annotation { "Feature Type Name" : "Feature", "Feature Type Description" : "" }
export const myFeature = defineFeature(function(context is Context, id is Id, definition is map)
    precondition{}
    {
        {
            var Q0;
            Q0=qCreatedBy(makeId("Top.planeOp"),FACE);
            var sketch = newSketch(context, id + "F0", { "sketchPlane" : qUnion([Q0])});
            skLineSegment(sketch, "E0.bottom", {"start": v(-906.5, 179.8) * mm, "end": v(731.8, 179.8) * mm});
            skLineSegment(sketch, "E0.top", {"start": v(-906.5, -706.02) * mm, "end": v(731.8, -706.02) * mm});
            skLineSegment(sketch, "E0.left", {"start": v(-906.5, 179.8) * mm, "end": v(-906.5, -706.02) * mm});
            skLineSegment(sketch, "E0.right", {"start": v(731.8, 179.8) * mm, "end": v(731.8, -706.02) * mm});
            skLineSegment(sketch, "E1.bottom", {"start": v(-379.45, 179.8) * mm, "end": v(-290.55, 179.8) * mm});
            skLineSegment(sketch, "E1.top", {"start": v(-379.45, -706.02) * mm, "end": v(-290.55, -706.02) * mm});
            skLineSegment(sketch, "E1.left", {"start": v(-379.45, 179.8) * mm, "end": v(-379.45, -706.02) * mm});
            skLineSegment(sketch, "E1.right", {"start": v(-290.55, 179.8) * mm, "end": v(-290.55, -706.02) * mm});
            skLineSegment(sketch, "E2.bottom", {"start": v(230.15, 179.8) * mm, "end": v(319.05, 179.8) * mm});
            skLineSegment(sketch, "E2.top", {"start": v(230.15, -706.02) * mm, "end": v(319.05, -706.02) * mm});
            skLineSegment(sketch, "E2.left", {"start": v(230.15, 179.8) * mm, "end": v(230.15, -706.02) * mm});
            skLineSegment(sketch, "E2.right", {"start": v(319.05, 179.8) * mm, "end": v(319.05, -706.02) * mm});
            skLineSegment(sketch, "E3.0", {"start": v(-919.2, 192.5) * mm, "end": v(744.5, 192.5) * mm});
            skLineSegment(sketch, "E3.1", {"start": v(-919.2, 192.5) * mm, "end": v(-919.2, -718.72) * mm});
            skLineSegment(sketch, "E3.2", {"start": v(-919.2, -718.72) * mm, "end": v(744.5, -718.72) * mm});
            skLineSegment(sketch, "E3.3", {"start": v(744.5, 192.5) * mm, "end": v(744.5, -718.72) * mm});
            skLineSegment(sketch, "E4", {"start": v(-906.5, -263.1) * mm, "end": v(731.8, -263.1) * mm, "construction": true});
            skLineSegment(sketch, "E5", {"start": v(-87.35, 192.5) * mm, "end": v(-87.35, -718.72) * mm, "construction": true});
            skLineSegment(sketch, "E6", {"start": v(-360.4, 192.5) * mm, "end": v(-360.4, -718.72) * mm, "construction": true});
            skLineSegment(sketch, "E7", {"start": v(185.7, 192.5) * mm, "end": v(185.7, -718.72) * mm, "construction": true});
            skSolve(sketch);
        }
        {
            var Q0;
            Q0=makeQuery(id+"F0.imprint","IMPRINT",FACE,{"disambiguationData":[TD([[makeQuery(id+"F0.imprint","IMPRINT",EDGE,{"derivedFrom":sQuery(id+"F0.wireOp",EDGE,"E1.bottom")}),-1.0]])]});
            var Q1;
            Q1=makeQuery(id+"F0.imprint","IMPRINT",FACE,{"disambiguationData":[TD([[makeQuery(id+"F0.imprint","IMPRINT",EDGE,{"derivedFrom":sQuery(id+"F0.wireOp",EDGE,"E2.bottom")}),-1.0]])]});
            var Q2;
            {var subQ1=sQuery(id+"F0.wireOp",EDGE,"E0.left");Q2=makeQuery(id+"F0.imprint","IMPRINT",FACE,{"disambiguationData":[TD([[makeQuery(id+"F0.imprint","IMPRINT",EDGE,{"derivedFrom":subQ1}),-1.0]])]});}
            extrude(context, id + "F1", {"entities" : qUnion([Q0, Q1, Q2]), "depth" : 88.9 * mm});
        }
        {
            var Q0;
            Q0=qCreatedBy(makeId("Top.planeOp"),FACE);
            var sketch = newSketch(context, id + "F2", { "sketchPlane" : qUnion([Q0])});
            skLineSegment(sketch, "E8.bottom", {"start": v(-914.83, 184.33) * mm, "end": v(738.67, 184.33) * mm});
            skLineSegment(sketch, "E8.top", {"start": v(-914.83, -709.72) * mm, "end": v(738.67, -709.72) * mm});
            skLineSegment(sketch, "E8.left", {"start": v(-914.83, 184.33) * mm, "end": v(-914.83, -709.72) * mm});
            skLineSegment(sketch, "E8.right", {"start": v(738.67, 184.33) * mm, "end": v(738.67, -709.72) * mm});
            skSolve(sketch);
        }
        {
            var Q0;
            Q0 = qSketchRegion(id + "F2", true);
            extrude(context, id + "F3", {"entities" : qUnion([Q0]), "oppositeDirection" : true, "depth" : 1.63 * mm});
        }
        {
            var Q0;
            Q0=qCreatedBy(makeId("Top.planeOp"),FACE);
            var sketch = newSketch(context, id + "F4", { "sketchPlane" : qUnion([Q0])});
            skLineSegment(sketch, "E9.bottom", {"start": v(-389.54, -366.33) * mm, "end": v(-713.39, -366.33) * mm});
            skLineSegment(sketch, "E9.top", {"start": v(-389.54, -156.78) * mm, "end": v(-624.62, -156.78) * mm});
            skLineSegment(sketch, "E9.left", {"start": v(-389.54, -366.33) * mm, "end": v(-389.54, -156.78) * mm});
            skLineSegment(sketch, "E9.right", {"start": v(-713.39, -366.33) * mm, "end": v(-713.39, -156.78) * mm});
            skCircle(sketch, "E10", {"center": v(-481.61, -261.55) * mm, "radius": 79.38 * mm});
            skLineSegment(sketch, "E11.top", {"start": v(-624.62, -193.13) * mm, "end": v(-687, -193.13) * mm});
            skLineSegment(sketch, "E11.left", {"start": v(-624.62, -156.78) * mm, "end": v(-624.62, -193.13) * mm});
            skLineSegment(sketch, "E11.right", {"start": v(-687, -156.78) * mm, "end": v(-687, -193.13) * mm});
            skLineSegment(sketch, "E12.trimOffspring", {"start": v(-687, -156.78) * mm, "end": v(-713.39, -156.78) * mm});
            skLineSegment(sketch, "E13.bottom", {"start": v(20.9, -171.42) * mm, "end": v(20.9, -495.27) * mm});
            skLineSegment(sketch, "E13.top", {"start": v(-188.66, -171.42) * mm, "end": v(-188.66, -406.5) * mm});
            skLineSegment(sketch, "E13.left", {"start": v(20.9, -171.42) * mm, "end": v(-188.66, -171.42) * mm});
            skLineSegment(sketch, "E13.right", {"start": v(20.9, -495.27) * mm, "end": v(-188.66, -495.27) * mm});
            skCircle(sketch, "E14", {"center": v(-83.88, -263.5) * mm, "radius": 79.38 * mm});
            skLineSegment(sketch, "E15.top", {"start": v(-152.3, -406.5) * mm, "end": v(-152.3, -468.9) * mm});
            skLineSegment(sketch, "E15.left", {"start": v(-188.66, -406.5) * mm, "end": v(-152.3, -406.5) * mm});
            skLineSegment(sketch, "E15.right", {"start": v(-188.66, -468.9) * mm, "end": v(-152.3, -468.9) * mm});
            skLineSegment(sketch, "E16.trimOffspring", {"start": v(-188.66, -468.9) * mm, "end": v(-188.66, -495.27) * mm});
            skSolve(sketch);
        }
        {
            var Q0;
            Q0=makeQuery(id+"F4.imprint","IMPRINT",FACE,{"disambiguationData":[TD([[makeQuery(id+"F4.imprint","IMPRINT",EDGE,{"derivedFrom":sQuery(id+"F4.wireOp",EDGE,"E9.bottom")}),-1.0]])]});
            var Q1;
            Q1=makeQuery(id+"F4.imprint","IMPRINT",FACE,{"disambiguationData":[TD([[makeQuery(id+"F4.imprint","IMPRINT",EDGE,{"derivedFrom":sQuery(id+"F4.wireOp",EDGE,"E13.bottom")}),-1.0]])]});
            extrude(context, id + "F5", {"entities" : qUnion([Q0, Q1]), "depth" : 171.45 * mm});
        }
        {
            var Q0;
            Q0=makeQuery(id+"F4.imprint","IMPRINT",FACE,{"disambiguationData":[TD([[makeQuery(id+"F4.imprint","IMPRINT",EDGE,{"derivedFrom":sQuery(id+"F4.wireOp",EDGE,"E14")}),1.0]])]});
            var Q1;
            Q1=makeQuery(id+"F4.imprint","IMPRINT",FACE,{"disambiguationData":[TD([[makeQuery(id+"F4.imprint","IMPRINT",EDGE,{"derivedFrom":sQuery(id+"F4.wireOp",EDGE,"E10")}),1.0]])]});
            extrude(context, id + "F6", {"entities" : qUnion([Q0, Q1]), "operationType" : NewBodyOperationType.REMOVE, "endBound" : BoundingType.THROUGH_ALL, "oppositeDirection" : true, "depth" : 25.4 * mm});
        }
        {
            var Q0;
            Q0=makeQuery(id+"F3.opExtrude","CAP_FACE",FACE,{"disambiguationData":[OSD([sQuery(id+"F2.wireOp",EDGE,"E8.bottom"),sQuery(id+"F2.wireOp",EDGE,"E8.top"),sQuery(id+"F2.wireOp",EDGE,"E8.left"),sQuery(id+"F2.wireOp",EDGE,"E8.right")])],"isStart":false});
            var sketch = newSketch(context, id + "F7", { "sketchPlane" : qUnion([Q0])});
            skText(sketch, "E17", { "text": "Shower Head", "fontName": "OpenSans-Regular.ttf"});
            const initialGuessF7  = {"E17": [0.5897, 0.62981, 0, -1, 0.0882]};
            skSetInitialGuess(sketch, initialGuessF7);
            skSolve(sketch);
        }
        {
            var Q0;
            Q0 = qSketchRegion(id + "F7", true);
            extrude(context, id + "F8", {"entities" : qUnion([Q0]), "operationType" : NewBodyOperationType.ADD, "depth" : 3.17 * mm});
        }
    });